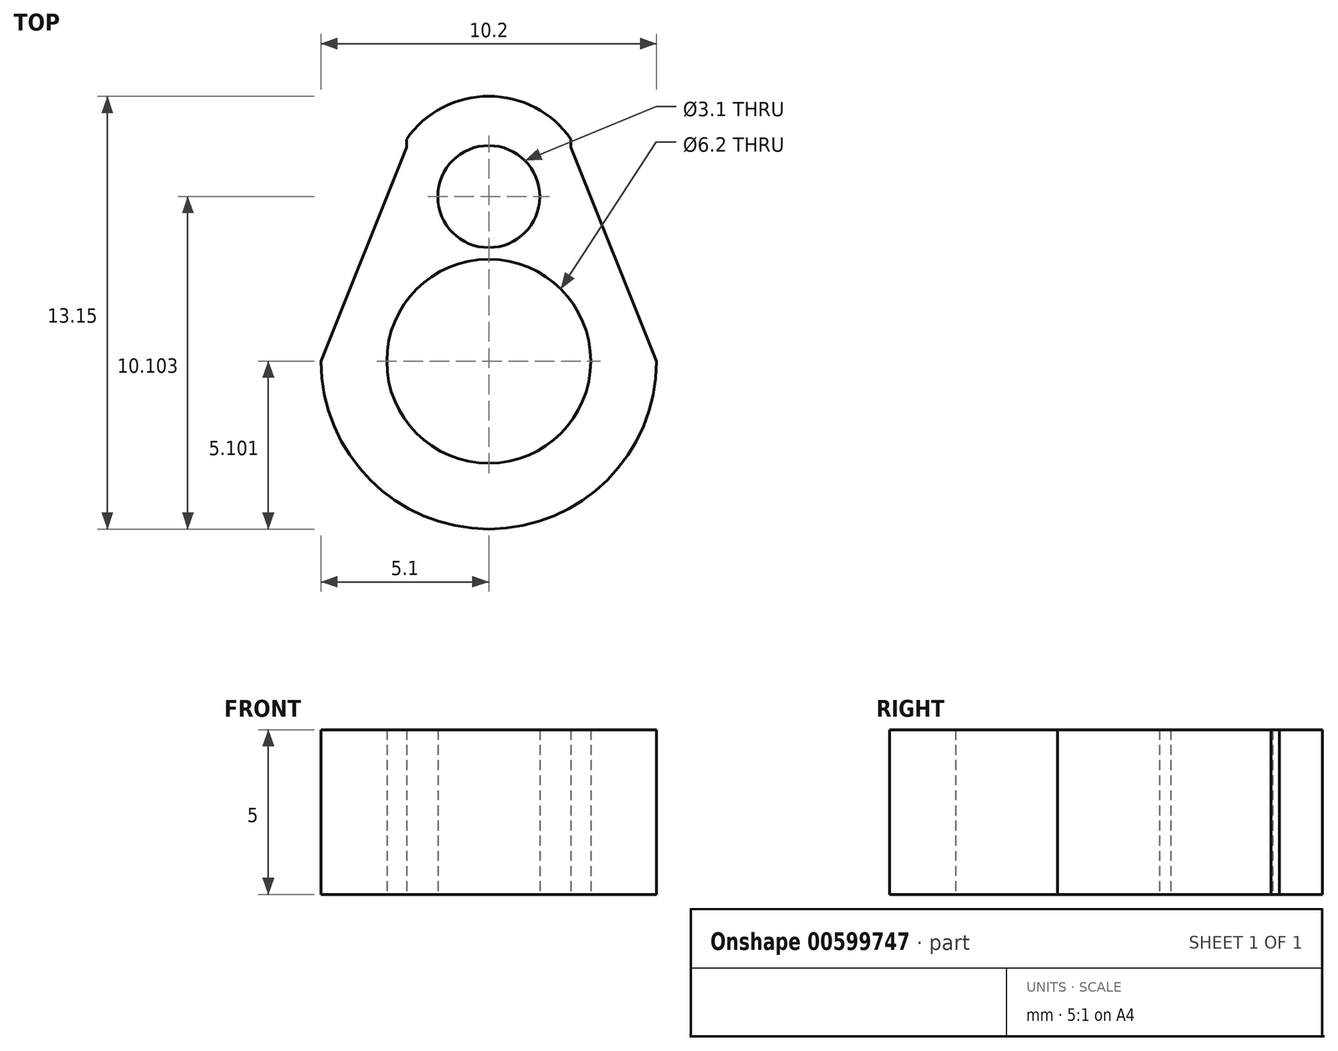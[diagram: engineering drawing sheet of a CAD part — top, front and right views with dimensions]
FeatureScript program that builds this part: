
annotation { "Feature Type Name" : "Feature", "Feature Type Description" : "" }
export const myFeature = defineFeature(function(context is Context, id is Id, definition is map)
    precondition{}
    {
        {
            var Q0;
            Q0=qCreatedBy(makeId("Top.planeOp"),FACE);
            var sketch = newSketch(context, id + "F0", { "sketchPlane" : qUnion([Q0])});
            skCircle(sketch, "E0", {"center": v(0, -1.5) * mm, "radius": 1.55 * mm});
            skArc(sketch, "E1", {"start": v(2.5, 0.25) * mm, "mid": v(0, 1.55) * mm, "end": v(-2.5, 0.25) * mm});
            skLineSegment(sketch, "E2", {"start": v(-2.5, 0.25) * mm, "end": v(-2.5, 0) * mm});
            skLineSegment(sketch, "E3", {"start": v(2.5, 0.25) * mm, "end": v(2.5, 0) * mm});
            skCircle(sketch, "E4", {"center": v(0, -6.5) * mm, "radius": 3.1 * mm});
            skArc(sketch, "E5", {"start": v(-5.1, -6.5) * mm, "mid": v(0, -11.6) * mm, "end": v(5.1, -6.5) * mm});
            skLineSegment(sketch, "E6", {"start": v(5.1, -6.5) * mm, "end": v(2.5, 0) * mm});
            skLineSegment(sketch, "E7", {"start": v(-5.1, -6.5) * mm, "end": v(-2.5, 0) * mm});
            skSolve(sketch);
        }
        {
            var Q0;
            Q0 = qSketchRegion(id + "F0", true);
            extrude(context, id + "F1", {"entities" : qUnion([Q0]), "depth" : 5 * mm, "offsetDistance" : 25 * mm});
        }
    });
